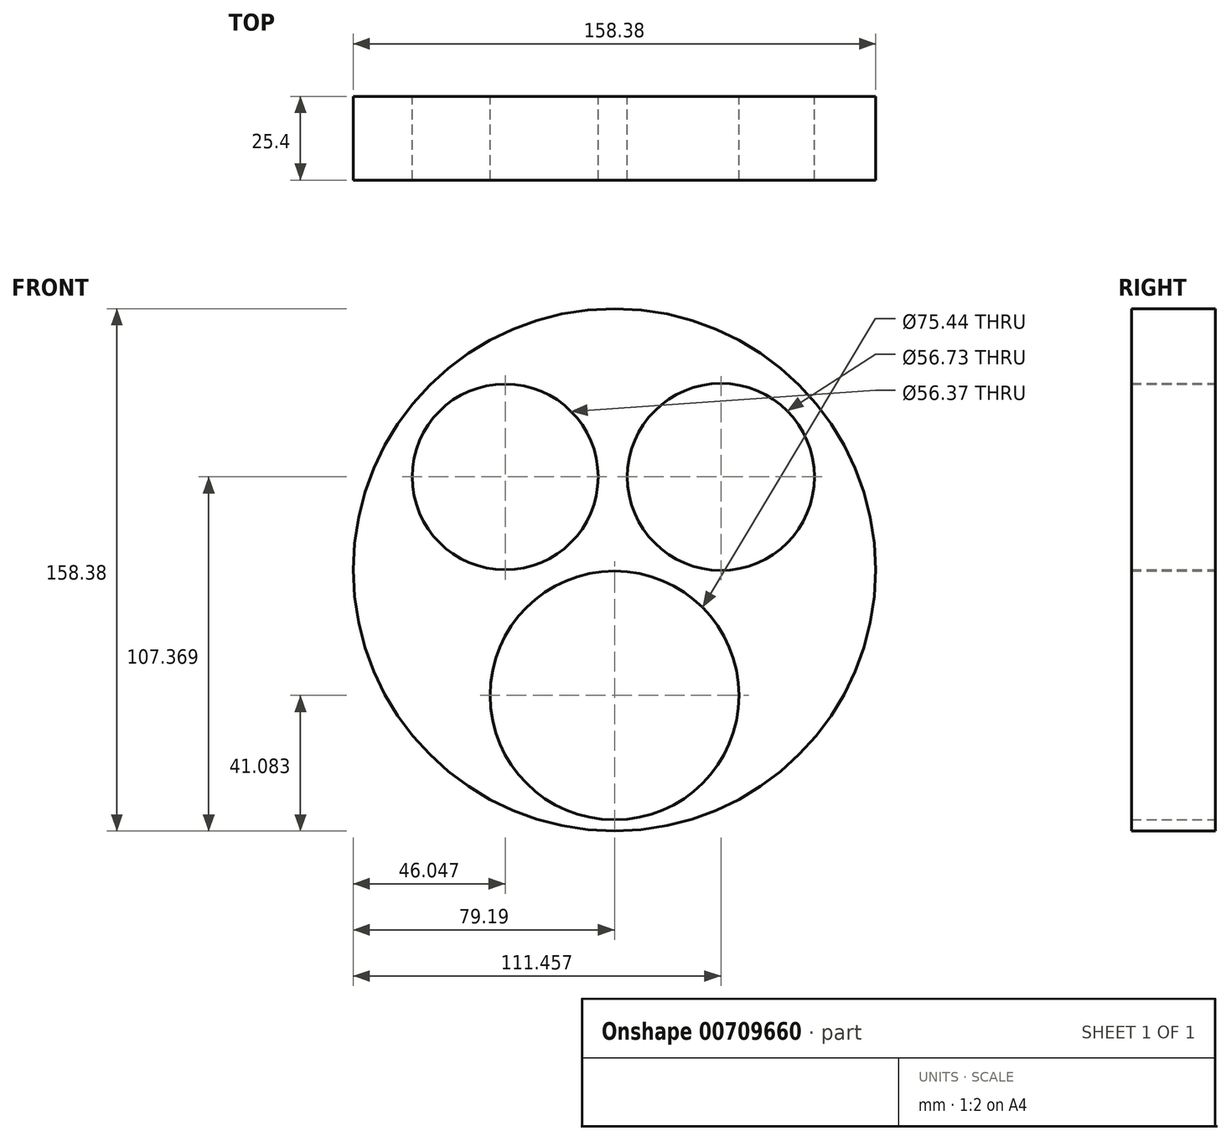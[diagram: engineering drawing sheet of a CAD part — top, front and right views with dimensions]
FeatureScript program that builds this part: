
annotation { "Feature Type Name" : "Feature", "Feature Type Description" : "" }
export const myFeature = defineFeature(function(context is Context, id is Id, definition is map)
    precondition{}
    {
        {
            var Q0;
            Q0=qCreatedBy(makeId("Front.planeOp"),FACE);
            var sketch = newSketch(context, id + "F0", { "sketchPlane" : qUnion([Q0])});
            skCircle(sketch, "E0", {"center": v(-33.14, 28.18) * mm, "radius": 28.18 * mm});
            skCircle(sketch, "E1", {"center": v(32.27, 28.18) * mm, "radius": 28.37 * mm});
            skCircle(sketch, "E2", {"center": v(0, -38.1) * mm, "radius": 37.72 * mm});
            skCircle(sketch, "E3", {"center": v(0, 0) * mm, "radius": 79.2 * mm});
            skSolve(sketch);
        }
        {
            var Q0;
            Q0=makeQuery(id+"F0.imprint","IMPRINT",FACE,{"disambiguationData":[TD([[makeQuery(id+"F0.imprint","IMPRINT",EDGE,{"derivedFrom":sQuery(id+"F0.wireOp",EDGE,"E0")}),-1.0]])]});
            extrude(context, id + "F1", {"entities" : qUnion([Q0]), "depth" : 25.4 * mm, "offsetDistance" : 25.4 * mm});
        }
    });
